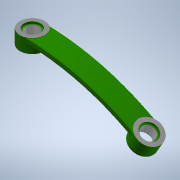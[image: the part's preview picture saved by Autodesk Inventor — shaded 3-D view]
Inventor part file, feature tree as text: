
AUTODESK INVENTOR PART (.ipt)
format: ipt  version: 2020.1 (Build 241239000, 239)  size: 303,104 bytes
history: native  units: mm
features: hole x6, sketch x5, plane x3, extrude x3, fillet x3, other x2, thicken_offset x1, revolve x1
ambient origin geometry x8: Origin, YZ Plane, XZ Plane, XY Plane, X Axis, Y Axis, Z Axis, Center Point
bodies: Solid1 (feature_tree)
feature tree (24):
  sketch  "3D Sketch1"
  plane  "Work Plane1"
  sketch  "Sketch2"  dims[d2=170.0mm d4=170.0mm]
  thicken_offset  "Thicken1"
  extrude  "Extrusion1"  TaperAngle=180.0deg  [1 undecoded]
  plane  "Work Plane2"
  extrude  "Extrusion2"  Depth=170.0mm
  plane  "Work Plane3"
  extrude  "Extrusion3"  Depth=4.0mm
  hole  "Hole1"  [1 undecoded]
  hole  "Hole2"  [1 undecoded]
  fillet  "Fillet1"  Radius=18.0mm
  fillet  "Fillet2"  Radius=10.0mm
  fillet  "Fillet3"  Radius=10.0mm
  hole  "Hole4"  [1 undecoded]
  hole  "Hole5"  [1 undecoded]
  hole  "Hole6"  [1 undecoded]
  hole  "Hole7"  [1 undecoded]
  sketch  "Sketch1"  dims[d0=170.0mm d1=180.0deg]
  other  "Srf1"
  sketch  "Sketch3"  dims[d5=16.0mm d6=4.0mm d7=8.0mm]
  sketch  "Sketch4"  dims[d8=10.0mm d9=0.0mm d10=18.0mm d11=10.0mm d12=0.0mm d13=18.0mm d14=10.0mm d15=0.0mm d16=10.0mm d17=10.0mm d18=10.0mm d19=6.0mm d20=4.0mm d21=2.0mm d22=90.0deg d23=8.0mm d24=20.594885mm d25=10.0mm d26=10.0mm d27=10.0mm d28=6.0mm d29=4.0mm d30=2.0mm d31=90.0deg d32=8.0mm d33=20.594885mm d34=1.0mm d35=10.0mm d36=0.7mm d52=30.0deg d53=10.0mm d54=10.0mm d55=12.0mm d56=6.0mm d57=4.0mm d58=2.0mm d59=90.0deg d60=1.5mm d61=0.0mm d62=10.0mm d63=10.0mm d64=12.0mm d65=6.0mm d66=4.0mm d67=2.0mm d68=90.0deg d69=1.5mm d70=0.0mm d71=10.0mm d72=10.0mm d73=12.0mm d74=6.0mm d75=4.0mm d76=2.0mm d77=90.0deg d78=1.5mm d79=0.0mm d80=10.0mm d81=10.0mm d82=12.0mm d83=6.0mm d84=4.0mm d85=2.0mm d86=90.0deg d87=1.5mm d88=0.0mm]
  revolve  "RevolutionSrf1"  Angle=30.0deg
  other  "3D Intersection1"
note: 7 required parameter values undecoded (feature->parameter linkage not recoverable at this tier; creation-order binding heuristic only, values carry confidence <= 0.55)
